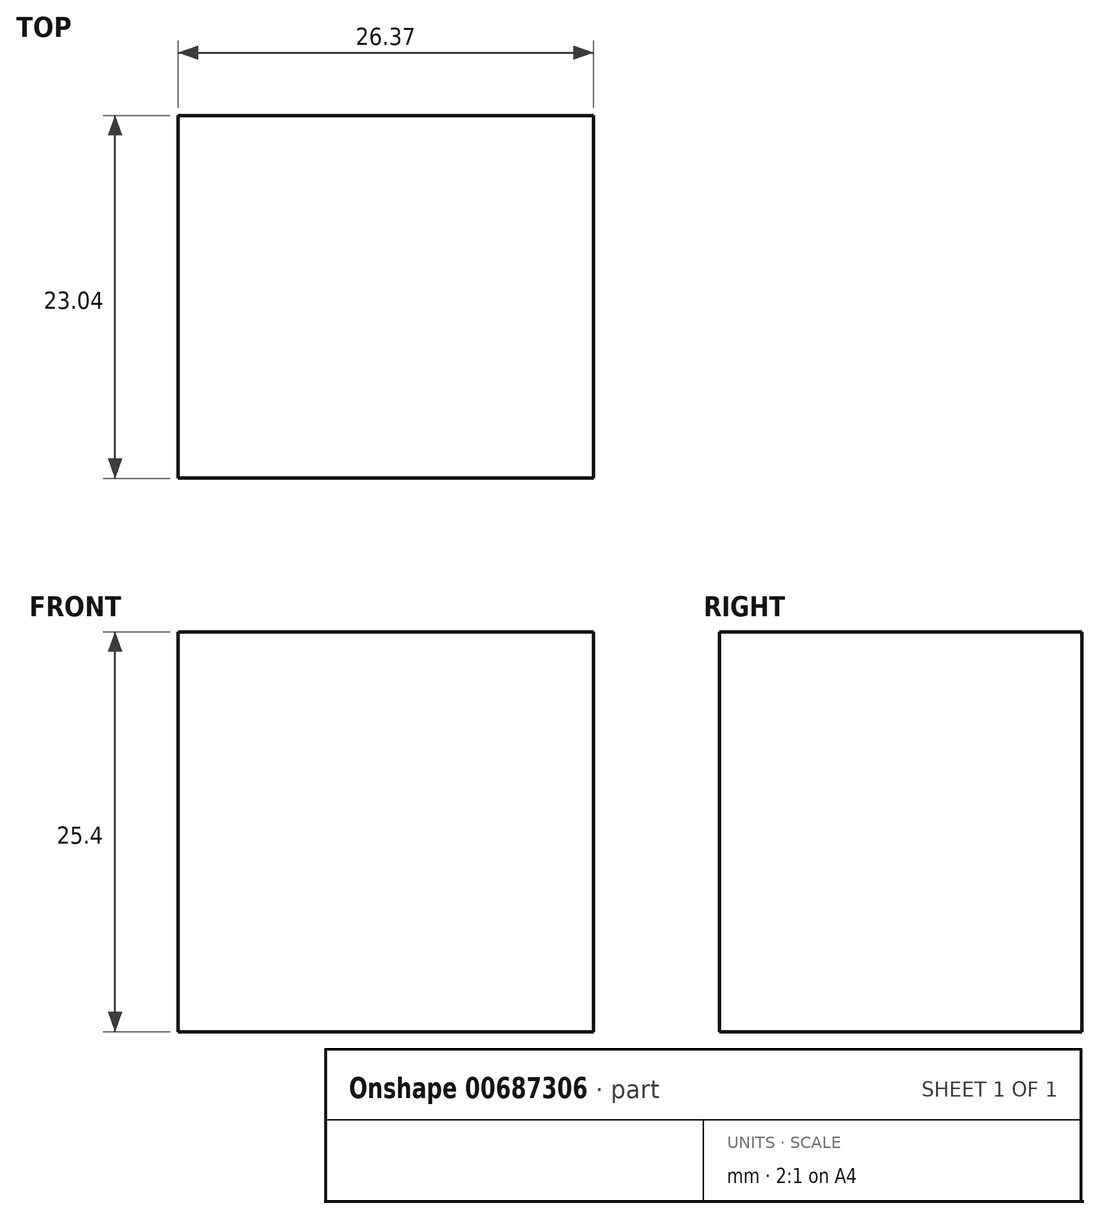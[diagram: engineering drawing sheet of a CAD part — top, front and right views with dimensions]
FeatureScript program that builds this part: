
annotation { "Feature Type Name" : "Feature", "Feature Type Description" : "" }
export const myFeature = defineFeature(function(context is Context, id is Id, definition is map)
    precondition{}
    {
        {
            var Q0;
            Q0=qCreatedBy(makeId("Top.planeOp"),FACE);
            var sketch = newSketch(context, id + "F0", { "sketchPlane" : qUnion([Q0])});
            skLineSegment(sketch, "E0.bottom", {"start": v(-14.7, 14.4) * mm, "end": v(11.67, 14.4) * mm});
            skLineSegment(sketch, "E0.top", {"start": v(-14.7, -8.64) * mm, "end": v(11.67, -8.64) * mm});
            skLineSegment(sketch, "E0.left", {"start": v(-14.7, 14.4) * mm, "end": v(-14.7, -8.64) * mm});
            skLineSegment(sketch, "E0.right", {"start": v(11.67, 14.4) * mm, "end": v(11.67, -8.64) * mm});
            skSolve(sketch);
        }
        {
            var Q0;
            Q0=makeQuery(id+"F0.imprint","IMPRINT",FACE,{"disambiguationData":[TD([[makeQuery(id+"F0.imprint","IMPRINT",EDGE,{"derivedFrom":sQuery(id+"F0.wireOp",EDGE,"E0.bottom")}),-1.0]])]});
            extrude(context, id + "F1", {"entities" : qUnion([Q0]), "depth" : 25.4 * mm, "offsetDistance" : 25.4 * mm});
        }
    });
